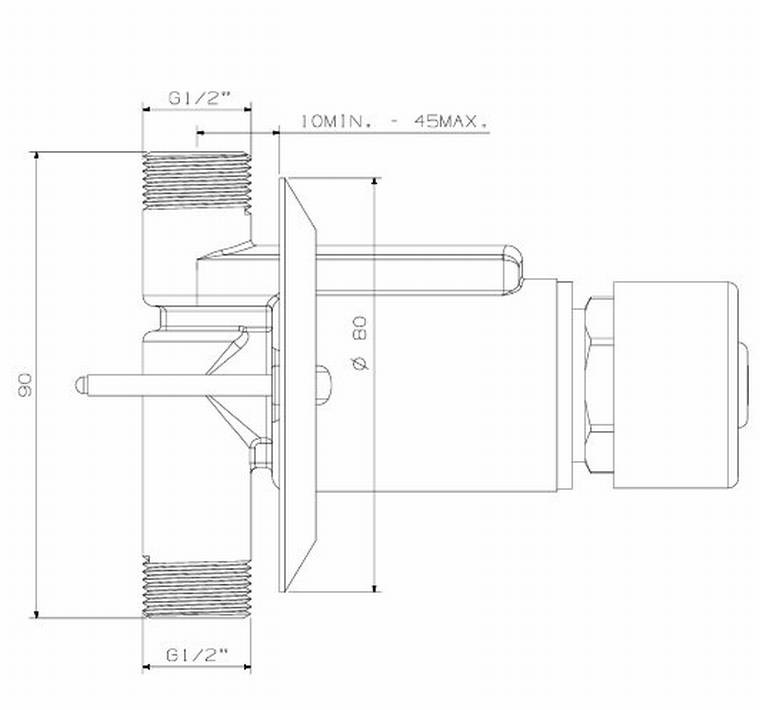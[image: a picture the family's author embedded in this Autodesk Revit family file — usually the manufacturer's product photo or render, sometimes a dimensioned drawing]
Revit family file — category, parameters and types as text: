
# Revit family: LIXIL - KM2-301 N - COBRA STOP TAP METERING
name_source: partatom
category: Plumbing Fixtures
units: mm (PartAtom-declared; Revit-internal decimal feet)

## family parameters
Always vertical = Yes
Cut with Voids When Loaded = No
Enable Cutting in Views = No
Maintain Annotation Orientation = No
OmniClass Number = 23.45.00.00
OmniClass Title = Sanitary, Laundry, and Cleaning Equipment
Part Type = Normal
Room Calculation Point = No
Round Connector Dimension = Use Diameter
Shared = Yes
Work Plane-Based = No

## types (1)
- KM2-301 N
    Default Elevation = 0 mm  [stored 0 ft]
    Description = Cobra stop tap metering mixer to detail and spec. See sanware schedule. Available from Lixil.
    Hosted on lixil.co.za = https://www.lixil.co.za
    M _ LOGO _ COBRA = M _ LIXIL - PLASTIC - BLUE 01
    M _ MIXER BODY = M _ LIXIL - CHROME 01
    M _ MIXER INDICATOR 01 = M _ LIXIL - PLASTIC - BLUE 01
    M _ MIXER LEVER = M _ LIXIL - CHROME 01
    Product Specification = Supplier: Lixil.
Product description: Non hold open, self closing. With stainless steel wall flange. 1/2BSP male iron connection ends. Flow cycle 1-20 seconds. 
Product Code: FSTAX1MT-0GT01.
SKU Code: KM2-301/N.
Barcode: 6002194032670.
Brand: Cobra
Range: Cobra.
Category: Plumbing Supplies
Sub-Category: Public Taps
Colour: Brushed Chrome
Package Height: 60 mm
Package Width: 100 mm
Package Length: 130 mm
Package Volume: 780000 mm³

Notes:
- Refer to manufacturer's and supplier's installation, maintenance and cleaning manual.
- Refer to manufacturer's and supplier's guarantees and warrantees document.

note: [stored X ft] marks values corroborated as IEEE doubles in the binary element streams (Revit-internal decimal feet)

## geometry (parser evidence)
native form markers: Sweep x10
no freeform markers — native parametric forms only
